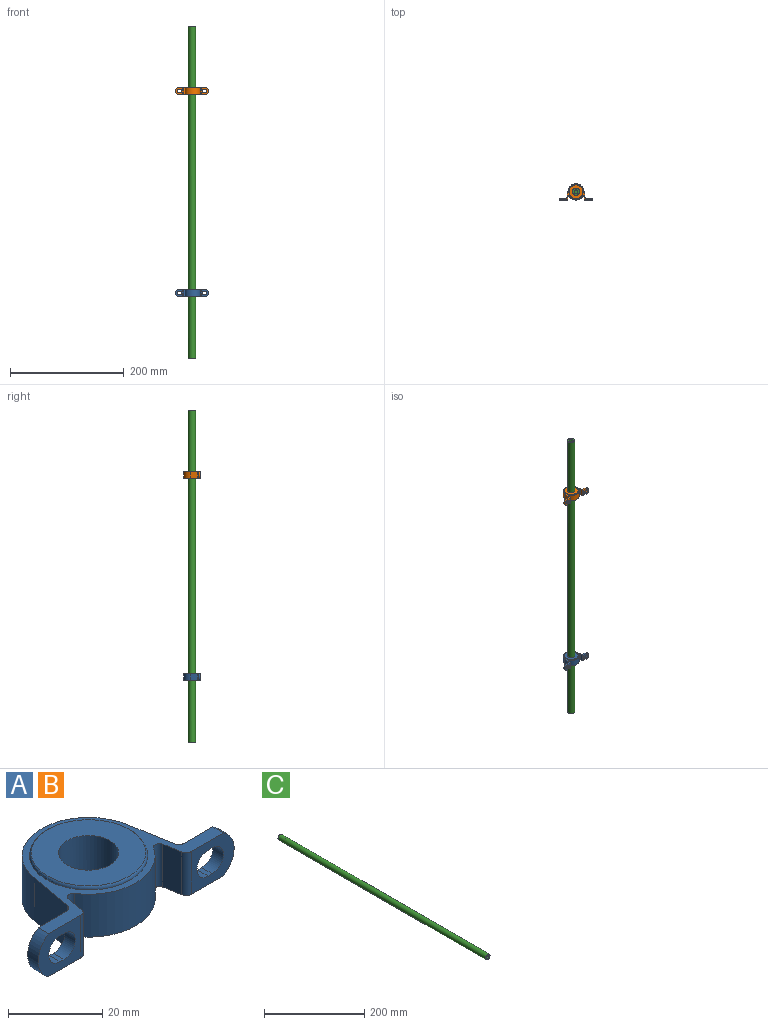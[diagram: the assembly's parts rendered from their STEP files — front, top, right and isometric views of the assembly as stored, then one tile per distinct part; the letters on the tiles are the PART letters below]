
ASSEMBLY  parts=3 mates=2
PART A: 33 faces, bbox 58.8x28.4x13.2 mm
  f0: plane 52.4x28.4mm, normal (0,0,-1), area 238.9mm2, adj f1,f7,f8,f13,f14,f15,f16,f17
  f1: torus R=11.52mm, axis (0,0,1), area 70.2mm2, adj f0,f2
  f2: plane 24.32x24.32mm, normal (0,0,-1), area 337.4mm2, adj f1,f3
  f3: cylinder r=6.36mm len=12.73mm, axis (0,0,1), area 507.7mm2, adj f2,f4
  f4: plane 24.32x24.32mm, normal (0,0,1), area 337.4mm2, adj f3,f5
  f5: torus R=11.52mm, axis (0,0,1), area 70.2mm2, adj f4,f6
  f6: plane 52.4x28.4mm, normal (0,0,1), area 238.9mm2, adj f5,f7,f8,f13,f14,f15,f16,f17
  f7: cylinder r=1.59mm len=11.13mm, axis (0,0,-1), area 24.7mm2, adj f0,f6,f8,f30
  f8: plane 12.8x11.13mm, normal (0,-1,0), area 88.2mm2, adj f0,f6,f7,f9,f10,f11,f12,f32
  f9: plane 3.18x1.19mm, normal (0,0,1), area 3.8mm2, adj f8,f10,f12,f13
  f10: cylinder r=3.38mm len=6.76mm, axis (0,1,0), area 33.7mm2, adj f8,f9,f11,f13
  f11: plane 3.18x1.19mm, normal (0,0,-1), area 3.8mm2, adj f8,f10,f12,f13
  f12: cylinder r=3.38mm len=6.76mm, axis (0,1,0), area 33.7mm2, adj f8,f9,f11,f13
  f13: plane 11.75x11.13mm, normal (0,1,0), area 76.4mm2, adj f0,f6,f9,f10,f11,f12,f14,f32
  f14: cylinder r=1.59mm len=11.13mm, axis (0,0,1), area 24.7mm2, adj f0,f6,f13,f15
  f15: plane 12.24x11.13mm, normal (-0.98,0.17,0), area 138.3mm2, adj f0,f6,f14,f16
  f16: cylinder r=14.12mm len=27.82mm, axis (0,0,1), area 438.7mm2, adj f0,f6,f15,f17
  f17: plane 12.24x11.13mm, normal (0.98,0.17,0), area 138.3mm2, adj f0,f6,f16,f18
  f18: cylinder r=1.59mm len=11.13mm, axis (0,0,1), area 24.7mm2, adj f0,f6,f17,f19
  f19: plane 11.75x11.13mm, normal (0,1,0), area 76.4mm2, adj f0,f6,f18,f20,f22,f23,f24,f31
  f20: cylinder r=3.38mm len=6.76mm, axis (0,1,0), area 33.7mm2, adj f19,f21,f22,f24
  f21: plane 12.8x11.13mm, normal (0,-1,0), area 88.2mm2, adj f0,f6,f20,f22,f23,f24,f25,f31
  f22: plane 3.18x1.19mm, normal (0,0,1), area 3.8mm2, adj f19,f20,f21,f23
  f23: cylinder r=3.38mm len=6.76mm, axis (0,1,0), area 33.7mm2, adj f19,f21,f22,f24
  f24: plane 3.18x1.19mm, normal (0,0,-1), area 3.8mm2, adj f19,f20,f21,f23
  f25: cylinder r=1.59mm len=11.13mm, axis (0,0,-1), area 24.7mm2, adj f0,f6,f21,f26
  f26: plane 11.13x4.81mm, normal (-0.98,-0.17,0), area 54.3mm2, adj f0,f6,f25,f27
  f27: cylinder r=1.27mm len=11.13mm, axis (0,0,1), area 33.8mm2, adj f0,f6,f26,f28
  f28: cylinder r=14.12mm len=23.7mm, axis (0,0,1), area 312.8mm2, adj f0,f6,f27,f29
  f29: cylinder r=1.27mm len=11.13mm, axis (0,0,1), area 33.8mm2, adj f0,f6,f28,f30
  f30: plane 11.13x4.81mm, normal (0.98,-0.17,0), area 54.3mm2, adj f0,f6,f7,f29
  f31: cylinder r=6.46mm len=11.13mm, axis (0,1,0), area 42.6mm2, adj f0,f6,f19,f21
  f32: cylinder r=6.46mm len=11.13mm, axis (0,1,0), area 42.6mm2, adj f0,f6,f8,f13
PART B: same geometry as A
PART C: 14 faces, bbox 12.7x584.2x12.7 mm
  f0: plane 12.7x12.7mm, normal (0,1,0), area 92.3mm2, adj f1,f5,f6,f7,f8,f9,f10,f12
  f1: cylinder r=6.35mm len=584.2mm, axis (0,1,0), area 23308.5mm2, adj f0,f2
  f2: plane 12.7x12.7mm, normal (0,-1,0), area 95mm2, adj f1,f3
  f3: cylinder r=3.17mm len=25.4mm, axis (0,1,0), area 506.7mm2, adj f2,f4
  f4: plane 6.35x6.35mm, normal (0,-1,0), area 31.7mm2, adj f3
  f5: plane 25.4x1.33mm, normal (-1,0,0), area 33.8mm2, adj f0,f7,f11,f12
  f6: plane 25.4x0.64mm, normal (-1,0,0), area 16.1mm2, adj f0,f10,f11,f12
  f7: plane 25.4x1.27mm, normal (0,0,-1), area 32.3mm2, adj f0,f5,f9,f11
  f8: plane 25.4x0.9mm, normal (1,0,0), area 22.9mm2, adj f0,f10,f11,f13
  f9: plane 25.4x1.6mm, normal (1,0,0), area 40.6mm2, adj f0,f7,f11,f13
  f10: plane 25.4x1.27mm, normal (0,0,1), area 32.3mm2, adj f0,f6,f8,f11
  f11: plane 8.32x6.35mm, normal (0,1,0), area 34.4mm2, adj f5,f6,f7,f8,f9,f10,f12,f13
  f12: cylinder r=3.17mm len=25.4mm, axis (0,1,0), area 253.4mm2, adj f0,f5,f6,f11
  f13: cylinder r=3.17mm len=25.4mm, axis (0,1,0), area 187mm2, adj f0,f8,f9,f11
PLACE A t=(-338.22,475.98,-466.57)mm
PLACE B t=(-338.22,475.98,-110.97)mm
PLACE C rot(axis=(-1,0,0),90deg) t=(-338.22,490.26,3.33)mm
MATE fastened B.f1 <-> C.f1  axis (0,0,1) through (-338.22,490.26,-104.62)mm
MATE fastened A.f1 <-> C.f1  axis (0,0,-1) through (-338.22,490.26,-472.92)mm
